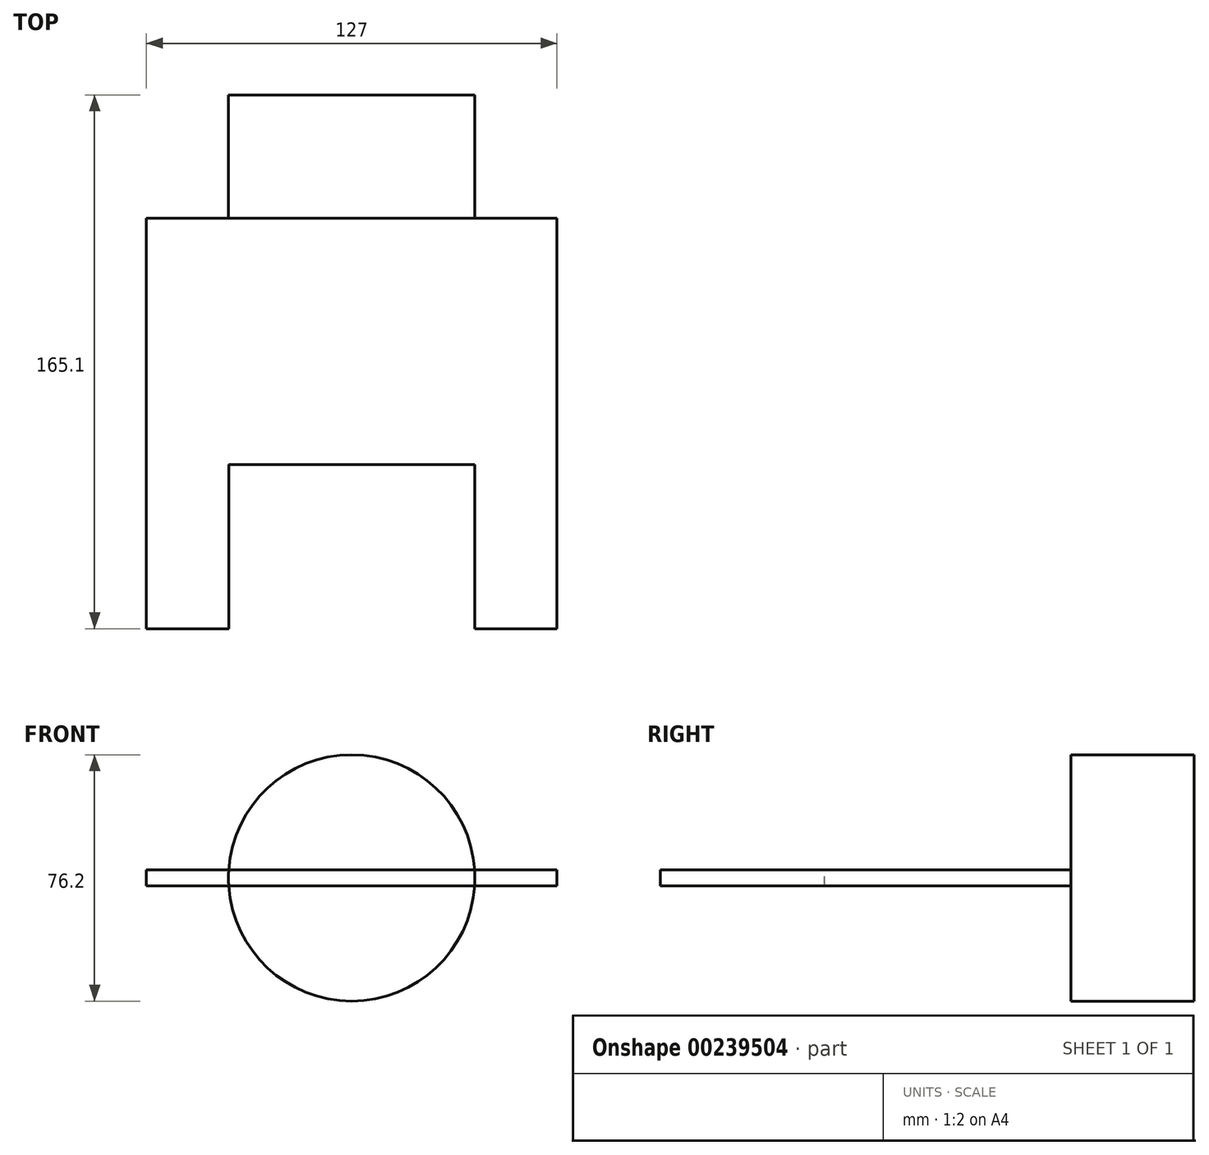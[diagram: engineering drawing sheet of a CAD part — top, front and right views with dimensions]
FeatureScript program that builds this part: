
annotation { "Feature Type Name" : "Feature", "Feature Type Description" : "" }
export const myFeature = defineFeature(function(context is Context, id is Id, definition is map)
    precondition{}
    {
        {
            assignVariable(context, id + "F0", {"name" : "L", "anyValue" : 5});
        }
        {
            var Q0;
            Q0=qCreatedBy(makeId("Top.planeOp"),FACE);
            var sketch = newSketch(context, id + "F1", { "sketchPlane" : qUnion([Q0])});
            skLineSegment(sketch, "E0.bottom", {"start": v(63.5, -63.5) * mm, "end": v(-63.5, -63.5) * mm});
            skLineSegment(sketch, "E0.top", {"start": v(63.5, 63.5) * mm, "end": v(-63.5, 63.5) * mm});
            skLineSegment(sketch, "E0.left", {"start": v(63.5, -63.5) * mm, "end": v(63.5, 63.5) * mm});
            skLineSegment(sketch, "E0.right", {"start": v(-63.5, -63.5) * mm, "end": v(-63.5, 63.5) * mm});
            skPoint(sketch, "E0.middle", {"position": v(0, 0) * mm});
            skSolve(sketch);
        }
        {
            var Q0;
            Q0 = qSketchRegion(id + "F1", true);
            extrude(context, id + "F2", {"entities" : qUnion([Q0]), "endBound" : BoundingType.SYMMETRIC, "depth" : (getVariable(context, 'L')) * mm});
        }
        {
            var Q0;
            Q0=makeQuery(id+"F2.opExtrude","SWEPT_FACE",FACE,{"disambiguationData":[OSD([sQuery(id+"F1.wireOp",EDGE,"E0.bottom")])]});
            var sketch = newSketch(context, id + "F3", { "sketchPlane" : qUnion([Q0])});
            skCircle(sketch, "E1", {"center": v(0, 0) * mm, "radius": 38.1 * mm});
            skSolve(sketch);
        }
        {
            var Q0;
            Q0=makeQuery(id+"F3.imprint","IMPRINT",FACE,{"disambiguationData":[TD([[makeQuery(id+"F3.imprint","IMPRINT",EDGE,{"derivedFrom":sQuery(id+"F3.wireOp",EDGE,"E1")}),1.0]])]});
            extrude(context, id + "F4", {"entities" : qUnion([Q0]), "operationType" : NewBodyOperationType.REMOVE, "oppositeDirection" : true, "depth" : 50.8 * mm});
        }
        {
            var Q0;
            Q0=makeQuery(id+"F2.opExtrude","SWEPT_FACE",FACE,{"disambiguationData":[OSD([sQuery(id+"F1.wireOp",EDGE,"E0.top")])]});
            var sketch = newSketch(context, id + "F5", { "sketchPlane" : qUnion([Q0])});
            skCircle(sketch, "E2.0", {"center": v(0, 0) * mm, "radius": 38.1 * mm});
            skSolve(sketch);
        }
        {
            var Q0;
            Q0 = qSketchRegion(id + "F5", true);
            extrude(context, id + "F6", {"entities" : qUnion([Q0]), "operationType" : NewBodyOperationType.ADD, "depth" : 38.1 * mm});
        }
    });
